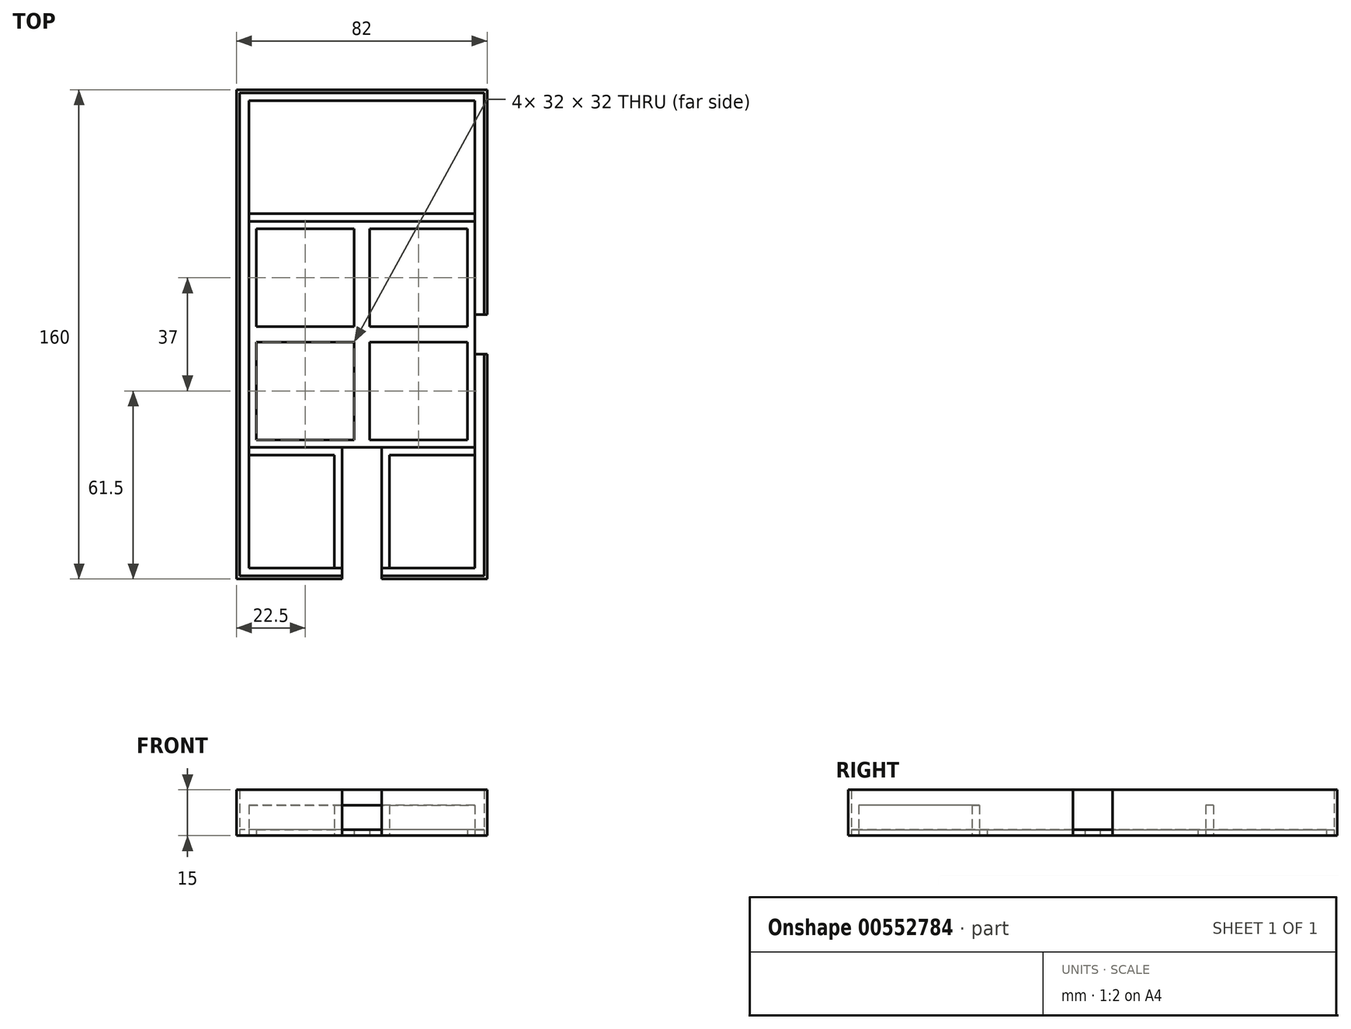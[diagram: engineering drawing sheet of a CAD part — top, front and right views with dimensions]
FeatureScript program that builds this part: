
annotation { "Feature Type Name" : "Feature", "Feature Type Description" : "" }
export const myFeature = defineFeature(function(context is Context, id is Id, definition is map)
    precondition{}
    {
        {
            var Q0;
            Q0=qCreatedBy(makeId("Top.planeOp"),FACE);
            var sketch = newSketch(context, id + "F0", { "sketchPlane" : qUnion([Q0])});
            skLineSegment(sketch, "E0.bottom", {"start": v(37, -37) * mm, "end": v(-37, -37) * mm});
            skLineSegment(sketch, "E0.top", {"start": v(37, 37) * mm, "end": v(-37, 37) * mm});
            skLineSegment(sketch, "E0.left", {"start": v(37, -37) * mm, "end": v(37, 37) * mm});
            skLineSegment(sketch, "E0.right", {"start": v(-37, -37) * mm, "end": v(-37, 37) * mm});
            skPoint(sketch, "E0.middle", {"position": v(0, 0) * mm});
            skLineSegment(sketch, "E1.bottom", {"start": v(40, -79) * mm, "end": v(-40, -79) * mm});
            skLineSegment(sketch, "E1.top", {"start": v(40, 79) * mm, "end": v(-40, 79) * mm});
            skLineSegment(sketch, "E1.left", {"start": v(40, -79) * mm, "end": v(40, 79) * mm});
            skLineSegment(sketch, "E1.right", {"start": v(-40, -79) * mm, "end": v(-40, 79) * mm});
            skLineSegment(sketch, "E2.bottom", {"start": v(-41, 80) * mm, "end": v(41, 80) * mm});
            skLineSegment(sketch, "E2.top", {"start": v(-41, -80) * mm, "end": v(41, -80) * mm});
            skLineSegment(sketch, "E2.left", {"start": v(-41, 80) * mm, "end": v(-41, -80) * mm});
            skLineSegment(sketch, "E2.right", {"start": v(41, 80) * mm, "end": v(41, -80) * mm});
            skLineSegment(sketch, "E3.bottom", {"start": v(-6.5, -37) * mm, "end": v(6.5, -37) * mm});
            skLineSegment(sketch, "E3.top", {"start": v(-6.5, -80) * mm, "end": v(6.5, -80) * mm});
            skLineSegment(sketch, "E3.left", {"start": v(-6.5, -37) * mm, "end": v(-6.5, -80) * mm});
            skLineSegment(sketch, "E3.right", {"start": v(6.5, -37) * mm, "end": v(6.5, -80) * mm});
            skLineSegment(sketch, "E4.bottom", {"start": v(37, 6.5) * mm, "end": v(41, 6.5) * mm});
            skLineSegment(sketch, "E4.top", {"start": v(37, -6.5) * mm, "end": v(41, -6.5) * mm});
            skLineSegment(sketch, "E4.left", {"start": v(37, 6.5) * mm, "end": v(37, -6.5) * mm});
            skLineSegment(sketch, "E4.right", {"start": v(41, 6.5) * mm, "end": v(41, -6.5) * mm});
            skLineSegment(sketch, "E5.bottom", {"start": v(-37, -39.5) * mm, "end": v(-9, -39.5) * mm});
            skLineSegment(sketch, "E5.top", {"start": v(-37, -76.5) * mm, "end": v(-9, -76.5) * mm});
            skLineSegment(sketch, "E5.left", {"start": v(-37, -39.5) * mm, "end": v(-37, -76.5) * mm});
            skLineSegment(sketch, "E5.right", {"start": v(-9, -39.5) * mm, "end": v(-9, -76.5) * mm});
            skLineSegment(sketch, "E6.MirrorCS", {"start": v(37, -76.5) * mm, "end": v(9, -76.5) * mm});
            skLineSegment(sketch, "E7.MirrorCS", {"start": v(37, -39.5) * mm, "end": v(9, -39.5) * mm});
            skLineSegment(sketch, "E8.MirrorCS", {"start": v(9, -39.5) * mm, "end": v(9, -76.5) * mm});
            skLineSegment(sketch, "E9.MirrorCS", {"start": v(37, -39.5) * mm, "end": v(37, -76.5) * mm});
            skLineSegment(sketch, "E10.bottom", {"start": v(-37, 76.5) * mm, "end": v(37, 76.5) * mm});
            skLineSegment(sketch, "E10.top", {"start": v(-37, 39.5) * mm, "end": v(37, 39.5) * mm});
            skLineSegment(sketch, "E10.left", {"start": v(-37, 76.5) * mm, "end": v(-37, 39.5) * mm});
            skLineSegment(sketch, "E10.right", {"start": v(37, 76.5) * mm, "end": v(37, 39.5) * mm});
            skLineSegment(sketch, "E11.bottom", {"start": v(-34.5, 34.5) * mm, "end": v(-2.5, 34.5) * mm});
            skLineSegment(sketch, "E11.top", {"start": v(-34.5, 2.5) * mm, "end": v(-2.5, 2.5) * mm});
            skLineSegment(sketch, "E11.left", {"start": v(-34.5, 34.5) * mm, "end": v(-34.5, 2.5) * mm});
            skLineSegment(sketch, "E11.right", {"start": v(-2.5, 34.5) * mm, "end": v(-2.5, 2.5) * mm});
            skLineSegment(sketch, "E12.MirrorCS", {"start": v(2.5, 34.5) * mm, "end": v(2.5, 2.5) * mm});
            skLineSegment(sketch, "E13.MirrorCS", {"start": v(34.5, 34.5) * mm, "end": v(2.5, 34.5) * mm});
            skLineSegment(sketch, "E14.MirrorCS", {"start": v(34.5, 34.5) * mm, "end": v(34.5, 2.5) * mm});
            skLineSegment(sketch, "E15.MirrorCS", {"start": v(34.5, 2.5) * mm, "end": v(2.5, 2.5) * mm});
            skLineSegment(sketch, "E16.MirrorCS", {"start": v(-34.5, -2.5) * mm, "end": v(-2.5, -2.5) * mm});
            skLineSegment(sketch, "E17.MirrorCS", {"start": v(34.5, -34.5) * mm, "end": v(2.5, -34.5) * mm});
            skLineSegment(sketch, "E18.MirrorCS", {"start": v(-34.5, -34.5) * mm, "end": v(-2.5, -34.5) * mm});
            skLineSegment(sketch, "E19.MirrorCS", {"start": v(2.5, -34.5) * mm, "end": v(2.5, -2.5) * mm});
            skLineSegment(sketch, "E20.MirrorCS", {"start": v(34.5, -2.5) * mm, "end": v(2.5, -2.5) * mm});
            skLineSegment(sketch, "E21.MirrorCS", {"start": v(-34.5, -34.5) * mm, "end": v(-34.5, -2.5) * mm});
            skLineSegment(sketch, "E22.MirrorCS", {"start": v(-2.5, -34.5) * mm, "end": v(-2.5, -2.5) * mm});
            skLineSegment(sketch, "E23.MirrorCS", {"start": v(34.5, -34.5) * mm, "end": v(34.5, -2.5) * mm});
            skLineSegment(sketch, "E24", {"start": v(-37, -39.5) * mm, "end": v(-37, -37) * mm});
            skLineSegment(sketch, "E25", {"start": v(37, -39.5) * mm, "end": v(37, -37) * mm});
            skLineSegment(sketch, "E26", {"start": v(-9, -76.5) * mm, "end": v(-6.5, -76.5) * mm});
            skLineSegment(sketch, "E27", {"start": v(9, -76.5) * mm, "end": v(6.5, -76.5) * mm});
            skLineSegment(sketch, "E28", {"start": v(37, 39.5) * mm, "end": v(37, 37) * mm});
            skLineSegment(sketch, "E29", {"start": v(-37, 39.5) * mm, "end": v(-37, 37) * mm});
            skSolve(sketch);
        }
        {
            var Q0;
            {var subQ4=sQuery(id+"F0.wireOp",EDGE,"E0.top");Q0=makeQuery(id+"F0.imprint","IMPRINT",FACE,{"disambiguationData":[TD([[makeQuery(id+"F0.imprint","IMPRINT",EDGE,{"derivedFrom":subQ4}),1.0]])]});}
            extrude(context, id + "F1", {"entities" : qUnion([Q0]), "depth" : 2 * mm, "offsetDistance" : 25 * mm});
        }
        {
            var Q0;
            {var subQ1=sQuery(id+"F0.wireOp",EDGE,"E1.top");Q0=makeQuery(id+"F0.imprint","IMPRINT",FACE,{"disambiguationData":[TD([[makeQuery(id+"F0.imprint","IMPRINT",EDGE,{"derivedFrom":subQ1}),-1.0]])]});}
            var Q1;
            {var subQ5=sQuery(id+"F0.wireOp",EDGE,"E1.left");var subQ6=sQuery(id+"F0.wireOp",EDGE,"E1.bottom");var subQ7=makeQuery(id+"F0.imprint","INTERSECT",VERTEX,{"derivedFrom":[subQ6,subQ5]});Q1=makeQuery(id+"F0.imprint","IMPRINT",FACE,{"disambiguationData":[TD([[makeQuery(id+"F0.imprint","IMPRINT",EDGE,{"disambiguationData":[TD([[subQ7,-1.0]])],"derivedFrom":subQ6}),1.0]])]});}
            extrude(context, id + "F2", {"entities" : qUnion([Q0, Q1]), "operationType" : NewBodyOperationType.ADD, "depth" : 15 * mm, "offsetDistance" : 25 * mm});
        }
        {
            var Q0;
            Q0=makeQuery(id+"F0.imprint","IMPRINT",FACE,{"disambiguationData":[TD([[makeQuery(id+"F0.imprint","IMPRINT",EDGE,{"derivedFrom":sQuery(id+"F0.wireOp",EDGE,"E0.right")}),1.0]])]});
            var Q1;
            Q1=makeQuery(id+"F0.imprint","IMPRINT",FACE,{"disambiguationData":[TD([[makeQuery(id+"F0.imprint","IMPRINT",EDGE,{"derivedFrom":sQuery(id+"F0.wireOp",EDGE,"E6.MirrorCS")}),1.0]])]});
            extrude(context, id + "F3", {"entities" : qUnion([Q0, Q1]), "depth" : 2 * mm, "offsetDistance" : 25 * mm});
        }
        {
            var Q0;
            Q0=makeQuery(id+"F0.imprint","IMPRINT",FACE,{"disambiguationData":[TD([[makeQuery(id+"F0.imprint","IMPRINT",EDGE,{"derivedFrom":sQuery(id+"F0.wireOp",EDGE,"E5.bottom")}),1.0]])]});
            var Q1;
            Q1=makeQuery(id+"F0.imprint","IMPRINT",FACE,{"disambiguationData":[TD([[makeQuery(id+"F0.imprint","IMPRINT",EDGE,{"derivedFrom":sQuery(id+"F0.wireOp",EDGE,"E7.MirrorCS")}),-1.0]])]});
            var Q2;
            Q2=makeQuery(id+"F0.imprint","IMPRINT",FACE,{"disambiguationData":[TD([[makeQuery(id+"F0.imprint","IMPRINT",EDGE,{"derivedFrom":sQuery(id+"F0.wireOp",EDGE,"E0.top")}),-1.0]])]});
            extrude(context, id + "F4", {"entities" : qUnion([Q0, Q1, Q2]), "depth" : 10 * mm, "offsetDistance" : 25 * mm});
        }
    });
